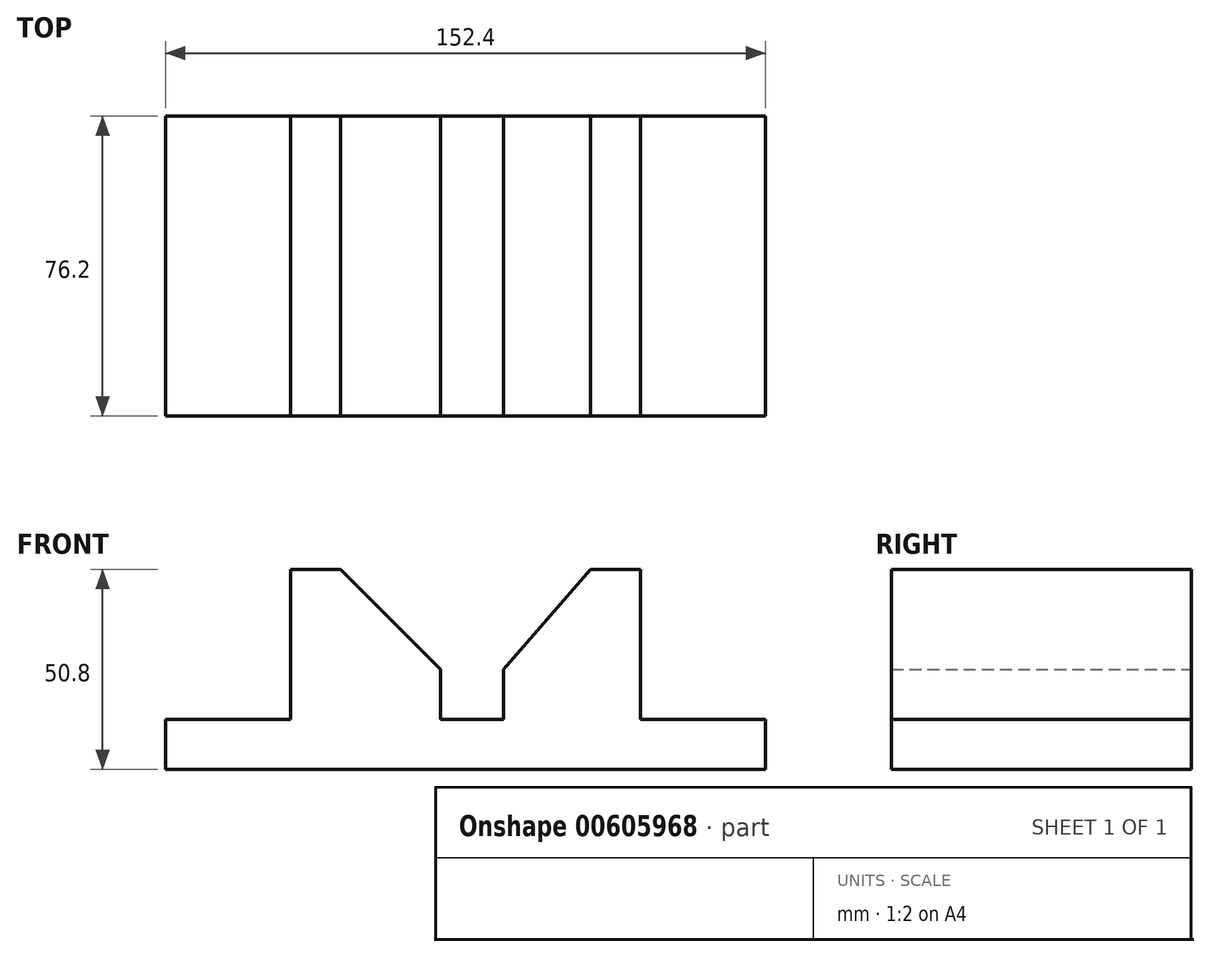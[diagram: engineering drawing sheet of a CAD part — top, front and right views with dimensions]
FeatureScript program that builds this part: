
annotation { "Feature Type Name" : "Feature", "Feature Type Description" : "" }
export const myFeature = defineFeature(function(context is Context, id is Id, definition is map)
    precondition{}
    {
        {
            var Q0;
            Q0=qCreatedBy(makeId("Front.planeOp"),FACE);
            var sketch = newSketch(context, id + "F0", { "sketchPlane" : qUnion([Q0])});
            skLineSegment(sketch, "E0", {"start": v(0, 0) * mm, "end": v(0, 12.7) * mm});
            skLineSegment(sketch, "E1", {"start": v(0, 0) * mm, "end": v(152.4, 0) * mm});
            skLineSegment(sketch, "E2", {"start": v(152.4, 0) * mm, "end": v(152.4, 12.7) * mm});
            skLineSegment(sketch, "E3", {"start": v(152.4, 12.7) * mm, "end": v(120.65, 12.7) * mm});
            skLineSegment(sketch, "E4", {"start": v(0, 12.7) * mm, "end": v(31.75, 12.7) * mm});
            skLineSegment(sketch, "E5", {"start": v(31.75, 12.7) * mm, "end": v(31.75, 50.8) * mm});
            skLineSegment(sketch, "E6", {"start": v(120.65, 12.7) * mm, "end": v(120.65, 50.8) * mm});
            skLineSegment(sketch, "E7", {"start": v(31.75, 50.8) * mm, "end": v(44.45, 50.8) * mm});
            skLineSegment(sketch, "E8", {"start": v(120.65, 50.8) * mm, "end": v(107.95, 50.8) * mm});
            skLineSegment(sketch, "E9", {"start": v(69.85, 12.7) * mm, "end": v(69.85, 25.4) * mm});
            skLineSegment(sketch, "E10", {"start": v(69.85, 25.4) * mm, "end": v(44.45, 50.8) * mm});
            skLineSegment(sketch, "E11", {"start": v(69.85, 12.7) * mm, "end": v(85.79, 12.7) * mm});
            skLineSegment(sketch, "E12", {"start": v(85.79, 12.7) * mm, "end": v(85.79, 25.4) * mm});
            skLineSegment(sketch, "E13", {"start": v(85.79, 25.4) * mm, "end": v(107.95, 50.8) * mm});
            skSolve(sketch);
        }
        {
            var Q0;
            Q0=makeQuery(id+"F0.imprint","IMPRINT",FACE,{"disambiguationData":[TD([[makeQuery(id+"F0.imprint","IMPRINT",EDGE,{"derivedFrom":sQuery(id+"F0.wireOp",EDGE,"E0")}),-1.0]])]});
            extrude(context, id + "F1", {"entities" : qUnion([Q0]), "depth" : 76.2 * mm, "offsetDistance" : 25.4 * mm});
        }
    });
